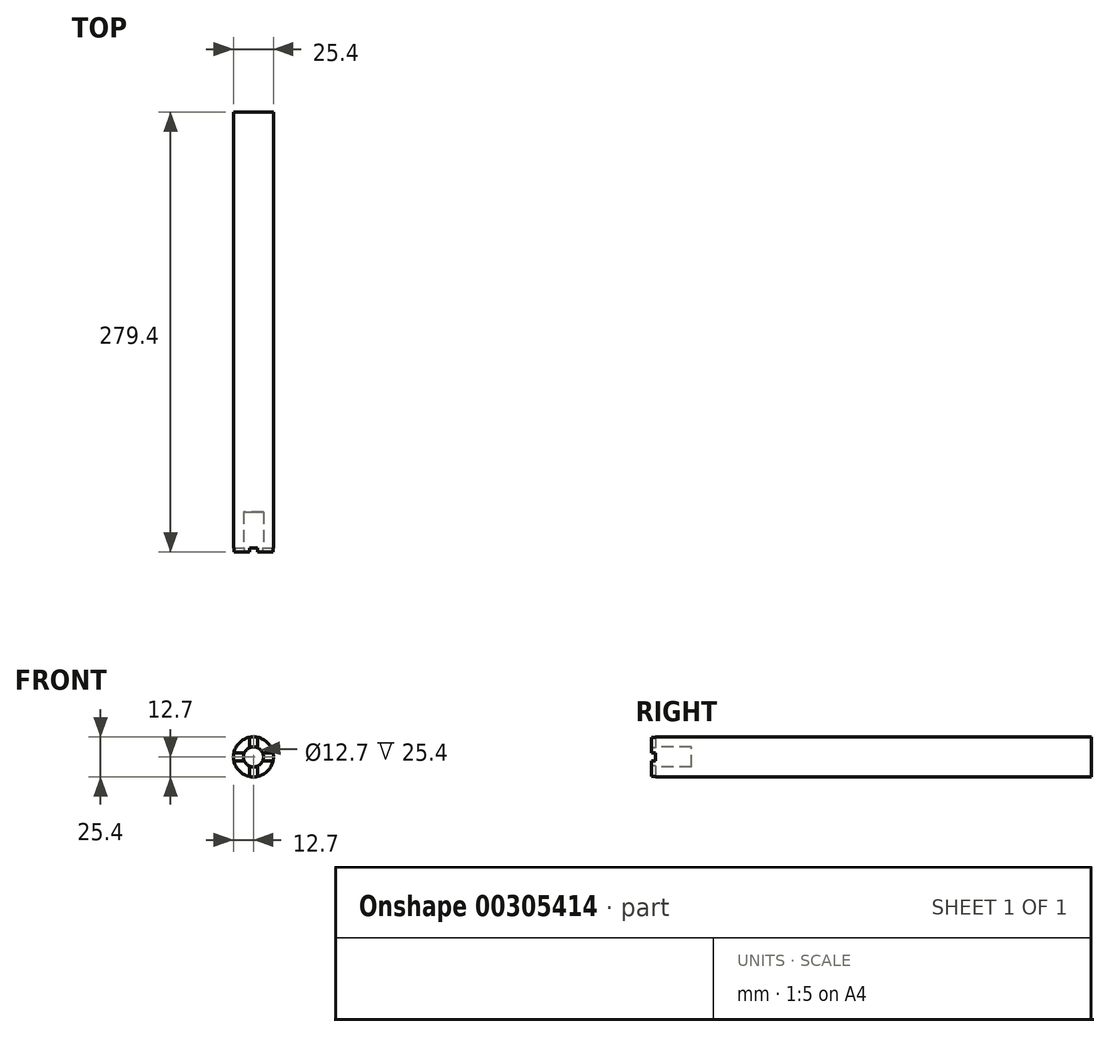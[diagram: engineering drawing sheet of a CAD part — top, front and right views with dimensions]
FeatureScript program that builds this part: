
annotation { "Feature Type Name" : "Feature", "Feature Type Description" : "" }
export const myFeature = defineFeature(function(context is Context, id is Id, definition is map)
    precondition{}
    {
        {
            var Q0;
            Q0=qCreatedBy(makeId("Front.planeOp"),FACE);
            var sketch = newSketch(context, id + "F0", { "sketchPlane" : qUnion([Q0])});
            skCircle(sketch, "E0", {"center": v(0, 0) * mm, "radius": 12.7 * mm});
            skSolve(sketch);
        }
        {
            var Q0;
            Q0 = qSketchRegion(id + "F0", true);
            extrude(context, id + "F1", {"entities" : qUnion([Q0]), "oppositeDirection" : true, "depth" : 279.4 * mm});
        }
        {
            var Q0;
            Q0=makeQuery(id+"F1.opExtrude","CAP_FACE",FACE,{"disambiguationData":[OSD([sQuery(id+"F0.wireOp",EDGE,"E0")])],"isStart":true});
            var sketch = newSketch(context, id + "F2", { "sketchPlane" : qUnion([Q0])});
            skLineSegment(sketch, "E1.bottom", {"start": v(-17.64, 2.54) * mm, "end": v(20.46, 2.54) * mm});
            skLineSegment(sketch, "E1.top", {"start": v(-17.64, -2.54) * mm, "end": v(20.46, -2.54) * mm});
            skLineSegment(sketch, "E1.left", {"start": v(-17.64, 2.54) * mm, "end": v(-17.64, -2.54) * mm});
            skLineSegment(sketch, "E1.right", {"start": v(20.46, 2.54) * mm, "end": v(20.46, -2.54) * mm});
            skSolve(sketch);
        }
        {
            var Q0;
            Q0 = qSketchRegion(id + "F2", true);
            extrude(context, id + "F3", {"entities" : qUnion([Q0]), "operationType" : NewBodyOperationType.REMOVE, "oppositeDirection" : true, "depth" : 2.54 * mm});
        }
        {
            var Q0;
            {var subQ0=sQuery(id+"F0.wireOp",EDGE,"E0");Q0=makeQuery(id+"F3.boolean.opBoolean","SPLIT",FACE,{"disambiguationData":[TD([makeQuery(id+"F3.opExtrude","SWEPT_FACE",FACE,{"disambiguationData":[OSD([sQuery(id+"F2.wireOp",EDGE,"E1.bottom")])]})])],"derivedFrom":makeQuery(id+"F1.opExtrude","CAP_FACE",FACE,{"disambiguationData":[OSD([subQ0])],"isStart":true})});}
            var sketch = newSketch(context, id + "F4", { "sketchPlane" : qUnion([Q0])});
            skLineSegment(sketch, "E2.bottom", {"start": v(-2.54, 22.2) * mm, "end": v(2.54, 22.2) * mm});
            skLineSegment(sketch, "E2.top", {"start": v(-2.54, -15.9) * mm, "end": v(2.54, -15.9) * mm});
            skLineSegment(sketch, "E2.left", {"start": v(-2.54, 22.2) * mm, "end": v(-2.54, -15.9) * mm});
            skLineSegment(sketch, "E2.right", {"start": v(2.54, 22.2) * mm, "end": v(2.54, -15.9) * mm});
            skSolve(sketch);
        }
        {
            var Q0;
            Q0 = qSketchRegion(id + "F4", true);
            extrude(context, id + "F5", {"entities" : qUnion([Q0]), "operationType" : NewBodyOperationType.REMOVE, "oppositeDirection" : true, "depth" : 2.54 * mm});
        }
        {
            var Q0;
            {var subQ0=sQuery(id+"F0.wireOp",EDGE,"E0");var subQ2=makeQuery(id+"F3.opExtrude","SWEPT_FACE",FACE,{"disambiguationData":[OSD([sQuery(id+"F2.wireOp",EDGE,"E1.bottom")])]});Q0=makeQuery(id+"F5.boolean.opBoolean","SPLIT",FACE,{"disambiguationData":[TD([makeQuery(id+"F5.opExtrude","SWEPT_FACE",FACE,{"disambiguationData":[OSD([sQuery(id+"F4.wireOp",EDGE,"E2.left")])]})])],"derivedFrom":makeQuery(id+"F3.boolean.opBoolean","SPLIT",FACE,{"disambiguationData":[TD([subQ2])],"derivedFrom":makeQuery(id+"F1.opExtrude","CAP_FACE",FACE,{"disambiguationData":[OSD([subQ0])],"isStart":true})})});}
            var sketch = newSketch(context, id + "F6", { "sketchPlane" : qUnion([Q0])});
            skCircle(sketch, "E3", {"center": v(0, 0) * mm, "radius": 6.35 * mm});
            skSolve(sketch);
        }
        {
            var Q0;
            Q0 = qSketchRegion(id + "F6", true);
            extrude(context, id + "F7", {"entities" : qUnion([Q0]), "operationType" : NewBodyOperationType.REMOVE, "oppositeDirection" : true, "depth" : 25.4 * mm});
        }
    });
